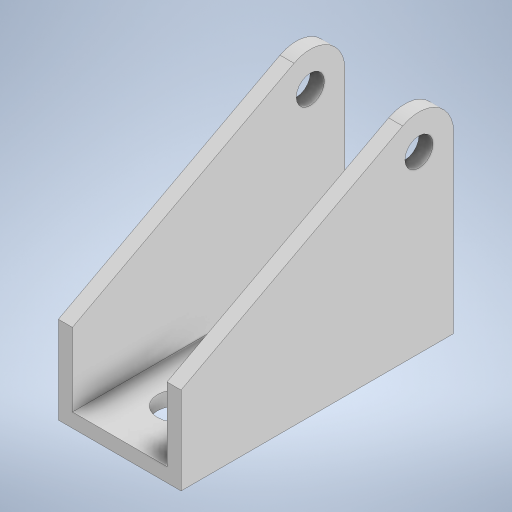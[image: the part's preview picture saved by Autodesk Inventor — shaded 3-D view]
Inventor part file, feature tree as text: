
AUTODESK INVENTOR PART (.ipt)
format: ipt  version: 2024 (Build 280153000, 153)  size: 242,688 bytes
history: native  units: mm
features: extrude x3, sketch x3, other x1
ambient origin geometry x8: Origin, YZ Plane, XZ Plane, XY Plane, X Axis, Y Axis, Z Axis, Center Point
bodies: Body1 (feature_tree)
feature tree (7):
  other  "솔리드1"
  extrude  "돌출1"  Depth=58.2mm
  extrude  "돌출2"  Depth=37.3mm
  extrude  "돌출3"  Depth=18.65mm
  sketch  "스케치1"
  sketch  "스케치2"
  sketch  "스케치3"
